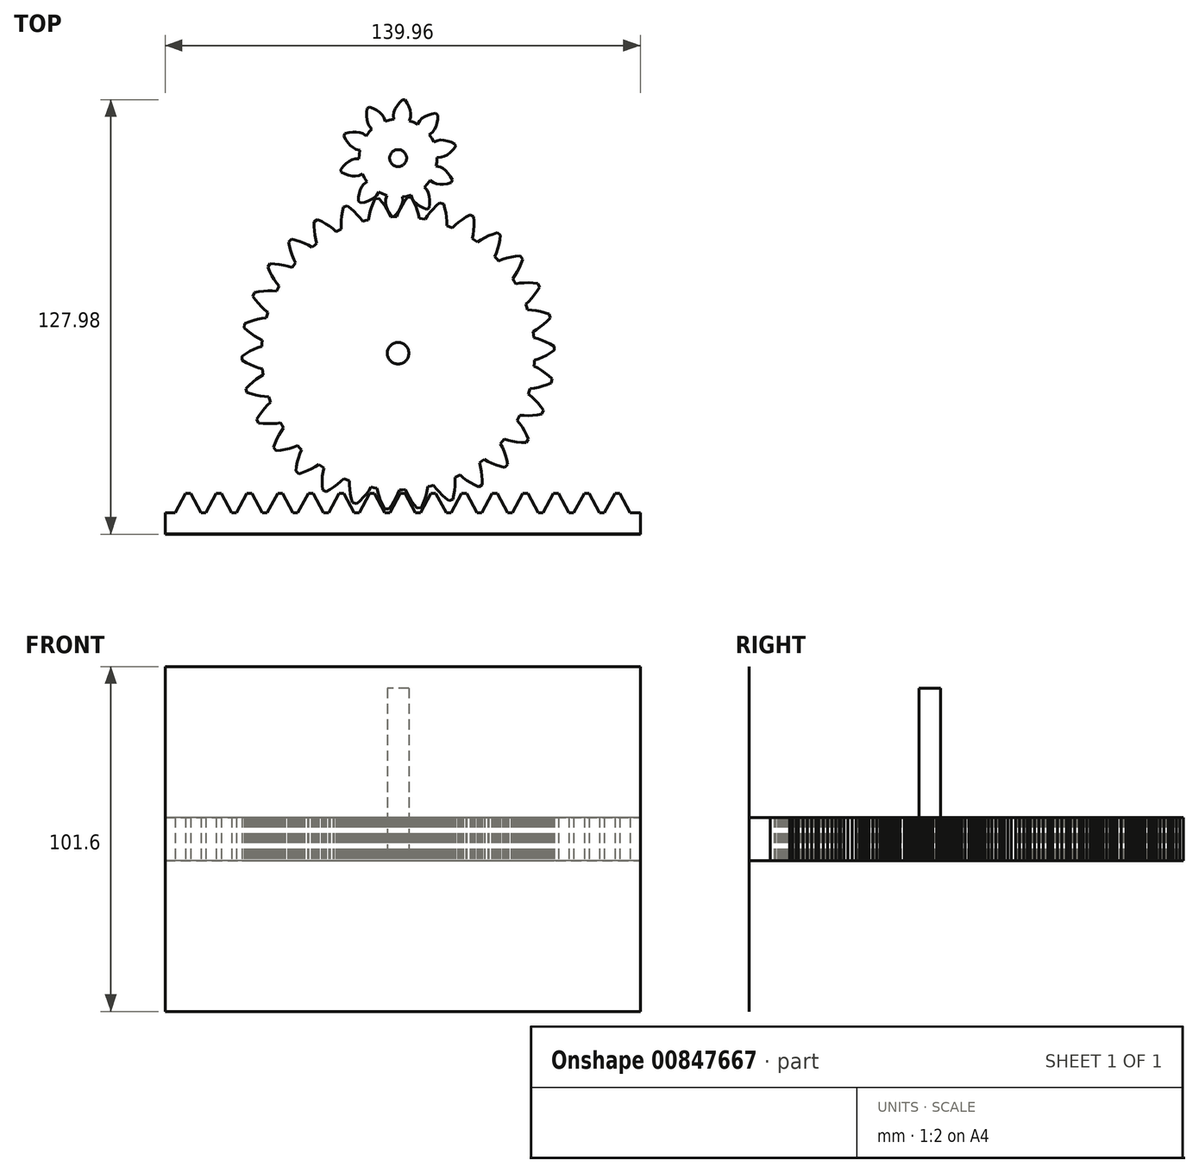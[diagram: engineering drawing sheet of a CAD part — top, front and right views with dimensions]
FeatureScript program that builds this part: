
annotation { "Feature Type Name" : "Feature", "Feature Type Description" : "" }
export const myFeature = defineFeature(function(context is Context, id is Id, definition is map)
    precondition{}
    {
        {
            var Q0;
            Q0=qCreatedBy(makeId("Top.planeOp"),FACE);
            var sketch = newSketch(context, id + "F0", { "sketchPlane" : qUnion([Q0])});
            skLineSegment(sketch, "E0", {"start": v(-1.74, 30.45) * mm, "end": v(-1.05, 31.36) * mm});
            skLineSegment(sketch, "E1", {"start": v(-1.05, 31.36) * mm, "end": v(-0.52, 32.3) * mm});
            skLineSegment(sketch, "E2", {"start": v(-0.52, 32.3) * mm, "end": v(-0.16, 33.24) * mm});
            skLineSegment(sketch, "E3", {"start": v(-0.16, 33.24) * mm, "end": v(-0.01, 34.16) * mm});
            skLineSegment(sketch, "E4", {"start": v(-0.01, 34.16) * mm, "end": v(-0.14, 35.35) * mm});
            skLineSegment(sketch, "E5", {"start": v(-0.14, 35.35) * mm, "end": v(1.13, 35.56) * mm});
            skLineSegment(sketch, "E6", {"start": v(1.13, 35.56) * mm, "end": v(1.13, 35.56) * mm});
            skLineSegment(sketch, "E7", {"start": v(1.13, 35.56) * mm, "end": v(1.15, 35.56) * mm});
            skLineSegment(sketch, "E8", {"start": v(1.15, 35.56) * mm, "end": v(1.17, 35.57) * mm});
            skLineSegment(sketch, "E9", {"start": v(1.17, 35.57) * mm, "end": v(1.17, 35.57) * mm});
            skLineSegment(sketch, "E10", {"start": v(1.17, 35.57) * mm, "end": v(2.41, 35.92) * mm});
            skLineSegment(sketch, "E11", {"start": v(2.41, 35.92) * mm, "end": v(2.8, 34.8) * mm});
            skLineSegment(sketch, "E12", {"start": v(2.8, 34.8) * mm, "end": v(3.33, 34.01) * mm});
            skLineSegment(sketch, "E13", {"start": v(3.33, 34.01) * mm, "end": v(4.06, 33.32) * mm});
            skLineSegment(sketch, "E14", {"start": v(4.06, 33.32) * mm, "end": v(4.94, 32.7) * mm});
            skLineSegment(sketch, "E15", {"start": v(4.94, 32.7) * mm, "end": v(5.95, 32.17) * mm});
            skLineSegment(sketch, "E16", {"start": v(5.95, 32.17) * mm, "end": v(7.07, 31.73) * mm});
            skLineSegment(sketch, "E17", {"start": v(7.07, 31.73) * mm, "end": v(7.77, 32.15) * mm});
            skLineSegment(sketch, "E18", {"start": v(7.77, 32.15) * mm, "end": v(7.93, 33.35) * mm});
            skLineSegment(sketch, "E19", {"start": v(7.93, 33.35) * mm, "end": v(7.95, 34.48) * mm});
            skLineSegment(sketch, "E20", {"start": v(7.95, 34.48) * mm, "end": v(7.84, 35.55) * mm});
            skLineSegment(sketch, "E21", {"start": v(7.84, 35.55) * mm, "end": v(7.58, 36.53) * mm});
            skLineSegment(sketch, "E22", {"start": v(7.58, 36.53) * mm, "end": v(7.15, 37.36) * mm});
            skLineSegment(sketch, "E23", {"start": v(7.15, 37.36) * mm, "end": v(6.35, 38.25) * mm});
            skLineSegment(sketch, "E24", {"start": v(6.35, 38.25) * mm, "end": v(7.25, 39.17) * mm});
            skLineSegment(sketch, "E25", {"start": v(7.25, 39.17) * mm, "end": v(7.26, 39.16) * mm});
            skLineSegment(sketch, "E26", {"start": v(7.26, 39.16) * mm, "end": v(7.27, 39.18) * mm});
            skLineSegment(sketch, "E27", {"start": v(7.27, 39.18) * mm, "end": v(7.28, 39.2) * mm});
            skLineSegment(sketch, "E28", {"start": v(7.28, 39.2) * mm, "end": v(7.28, 39.2) * mm});
            skLineSegment(sketch, "E29", {"start": v(7.28, 39.2) * mm, "end": v(8.08, 40.21) * mm});
            skLineSegment(sketch, "E30", {"start": v(8.08, 40.21) * mm, "end": v(9.06, 39.53) * mm});
            skLineSegment(sketch, "E31", {"start": v(9.06, 39.53) * mm, "end": v(9.94, 39.2) * mm});
            skLineSegment(sketch, "E32", {"start": v(9.94, 39.2) * mm, "end": v(10.94, 39.07) * mm});
            skLineSegment(sketch, "E33", {"start": v(10.94, 39.07) * mm, "end": v(12.01, 39.09) * mm});
            skLineSegment(sketch, "E34", {"start": v(12.01, 39.09) * mm, "end": v(13.14, 39.25) * mm});
            skLineSegment(sketch, "E35", {"start": v(13.14, 39.25) * mm, "end": v(14.3, 39.56) * mm});
            skLineSegment(sketch, "E36", {"start": v(14.3, 39.56) * mm, "end": v(14.63, 40.31) * mm});
            skLineSegment(sketch, "E37", {"start": v(14.63, 40.31) * mm, "end": v(14.06, 41.37) * mm});
            skLineSegment(sketch, "E38", {"start": v(14.06, 41.37) * mm, "end": v(13.4, 42.3) * mm});
            skLineSegment(sketch, "E39", {"start": v(13.4, 42.3) * mm, "end": v(12.68, 43.1) * mm});
            skLineSegment(sketch, "E40", {"start": v(12.68, 43.1) * mm, "end": v(11.9, 43.74) * mm});
            skLineSegment(sketch, "E41", {"start": v(11.9, 43.74) * mm, "end": v(11.06, 44.16) * mm});
            skLineSegment(sketch, "E42", {"start": v(11.06, 44.16) * mm, "end": v(9.9, 44.4) * mm});
            skLineSegment(sketch, "E43", {"start": v(9.9, 44.4) * mm, "end": v(10.09, 45.68) * mm});
            skLineSegment(sketch, "E44", {"start": v(10.09, 45.68) * mm, "end": v(10.09, 45.68) * mm});
            skLineSegment(sketch, "E45", {"start": v(10.09, 45.68) * mm, "end": v(10.1, 45.7) * mm});
            skLineSegment(sketch, "E46", {"start": v(10.1, 45.7) * mm, "end": v(10.1, 45.72) * mm});
            skLineSegment(sketch, "E47", {"start": v(10.1, 45.72) * mm, "end": v(10.1, 45.72) * mm});
            skLineSegment(sketch, "E48", {"start": v(10.1, 45.72) * mm, "end": v(10.14, 47.01) * mm});
            skLineSegment(sketch, "E49", {"start": v(10.14, 47.01) * mm, "end": v(11.33, 47.03) * mm});
            skLineSegment(sketch, "E50", {"start": v(11.33, 47.03) * mm, "end": v(12.24, 47.3) * mm});
            skLineSegment(sketch, "E51", {"start": v(12.24, 47.3) * mm, "end": v(13.12, 47.77) * mm});
            skLineSegment(sketch, "E52", {"start": v(13.12, 47.77) * mm, "end": v(13.98, 48.42) * mm});
            skLineSegment(sketch, "E53", {"start": v(13.98, 48.42) * mm, "end": v(14.8, 49.21) * mm});
            skLineSegment(sketch, "E54", {"start": v(14.8, 49.21) * mm, "end": v(15.56, 50.14) * mm});
            skLineSegment(sketch, "E55", {"start": v(15.56, 50.14) * mm, "end": v(15.38, 50.94) * mm});
            skLineSegment(sketch, "E56", {"start": v(15.38, 50.94) * mm, "end": v(14.3, 51.46) * mm});
            skLineSegment(sketch, "E57", {"start": v(14.3, 51.46) * mm, "end": v(13.22, 51.83) * mm});
            skLineSegment(sketch, "E58", {"start": v(13.22, 51.83) * mm, "end": v(12.17, 52.05) * mm});
            skLineSegment(sketch, "E59", {"start": v(12.17, 52.05) * mm, "end": v(11.16, 52.1) * mm});
            skLineSegment(sketch, "E60", {"start": v(11.16, 52.1) * mm, "end": v(10.23, 51.96) * mm});
            skLineSegment(sketch, "E61", {"start": v(10.23, 51.96) * mm, "end": v(9.14, 51.47) * mm});
            skLineSegment(sketch, "E62", {"start": v(9.14, 51.47) * mm, "end": v(8.55, 52.62) * mm});
            skLineSegment(sketch, "E63", {"start": v(8.55, 52.62) * mm, "end": v(8.55, 52.62) * mm});
            skLineSegment(sketch, "E64", {"start": v(8.55, 52.62) * mm, "end": v(8.54, 52.63) * mm});
            skLineSegment(sketch, "E65", {"start": v(8.54, 52.63) * mm, "end": v(8.53, 52.65) * mm});
            skLineSegment(sketch, "E66", {"start": v(8.53, 52.65) * mm, "end": v(8.53, 52.65) * mm});
            skLineSegment(sketch, "E67", {"start": v(8.53, 52.65) * mm, "end": v(7.81, 53.72) * mm});
            skLineSegment(sketch, "E68", {"start": v(7.81, 53.72) * mm, "end": v(8.76, 54.44) * mm});
            skLineSegment(sketch, "E69", {"start": v(8.76, 54.44) * mm, "end": v(9.34, 55.18) * mm});
            skLineSegment(sketch, "E70", {"start": v(9.34, 55.18) * mm, "end": v(9.78, 56.1) * mm});
            skLineSegment(sketch, "E71", {"start": v(9.78, 56.1) * mm, "end": v(10.1, 57.12) * mm});
            skLineSegment(sketch, "E72", {"start": v(10.1, 57.12) * mm, "end": v(10.29, 58.24) * mm});
            skLineSegment(sketch, "E73", {"start": v(10.29, 58.24) * mm, "end": v(10.35, 59.44) * mm});
            skLineSegment(sketch, "E74", {"start": v(10.35, 59.44) * mm, "end": v(9.74, 59.98) * mm});
            skLineSegment(sketch, "E75", {"start": v(9.74, 59.98) * mm, "end": v(8.56, 59.77) * mm});
            skLineSegment(sketch, "E76", {"start": v(8.56, 59.77) * mm, "end": v(7.47, 59.43) * mm});
            skLineSegment(sketch, "E77", {"start": v(7.47, 59.43) * mm, "end": v(6.49, 59) * mm});
            skLineSegment(sketch, "E78", {"start": v(6.49, 59) * mm, "end": v(5.64, 58.45) * mm});
            skLineSegment(sketch, "E79", {"start": v(5.64, 58.45) * mm, "end": v(4.98, 57.78) * mm});
            skLineSegment(sketch, "E80", {"start": v(4.98, 57.78) * mm, "end": v(4.38, 56.75) * mm});
            skLineSegment(sketch, "E81", {"start": v(4.38, 56.75) * mm, "end": v(3.23, 57.32) * mm});
            skLineSegment(sketch, "E82", {"start": v(3.23, 57.32) * mm, "end": v(3.23, 57.33) * mm});
            skLineSegment(sketch, "E83", {"start": v(3.23, 57.33) * mm, "end": v(3.21, 57.33) * mm});
            skLineSegment(sketch, "E84", {"start": v(3.21, 57.33) * mm, "end": v(3.2, 57.34) * mm});
            skLineSegment(sketch, "E85", {"start": v(3.2, 57.34) * mm, "end": v(3.2, 57.34) * mm});
            skLineSegment(sketch, "E86", {"start": v(3.2, 57.34) * mm, "end": v(1.98, 57.78) * mm});
            skLineSegment(sketch, "E87", {"start": v(1.98, 57.78) * mm, "end": v(2.33, 58.93) * mm});
            skLineSegment(sketch, "E88", {"start": v(2.33, 58.93) * mm, "end": v(2.36, 59.87) * mm});
            skLineSegment(sketch, "E89", {"start": v(2.36, 59.87) * mm, "end": v(2.18, 60.86) * mm});
            skLineSegment(sketch, "E90", {"start": v(2.18, 60.86) * mm, "end": v(1.83, 61.87) * mm});
            skLineSegment(sketch, "E91", {"start": v(1.83, 61.87) * mm, "end": v(1.33, 62.9) * mm});
            skLineSegment(sketch, "E92", {"start": v(1.33, 62.9) * mm, "end": v(0.67, 63.9) * mm});
            skLineSegment(sketch, "E93", {"start": v(0.67, 63.9) * mm, "end": v(-0.14, 63.99) * mm});
            skLineSegment(sketch, "E94", {"start": v(-0.14, 63.99) * mm, "end": v(-0.97, 63.11) * mm});
            skLineSegment(sketch, "E95", {"start": v(-0.97, 63.11) * mm, "end": v(-1.66, 62.2) * mm});
            skLineSegment(sketch, "E96", {"start": v(-1.66, 62.2) * mm, "end": v(-2.19, 61.27) * mm});
            skLineSegment(sketch, "E97", {"start": v(-2.19, 61.27) * mm, "end": v(-2.55, 60.33) * mm});
            skLineSegment(sketch, "E98", {"start": v(-2.55, 60.33) * mm, "end": v(-2.7, 59.4) * mm});
            skLineSegment(sketch, "E99", {"start": v(-2.7, 59.4) * mm, "end": v(-2.57, 58.22) * mm});
            skLineSegment(sketch, "E100", {"start": v(-2.57, 58.22) * mm, "end": v(-3.84, 58) * mm});
            skLineSegment(sketch, "E101", {"start": v(-3.84, 58) * mm, "end": v(-3.84, 58) * mm});
            skLineSegment(sketch, "E102", {"start": v(-3.84, 58) * mm, "end": v(-3.86, 58) * mm});
            skLineSegment(sketch, "E103", {"start": v(-3.86, 58) * mm, "end": v(-3.88, 58) * mm});
            skLineSegment(sketch, "E104", {"start": v(-3.88, 58) * mm, "end": v(-3.88, 58) * mm});
            skLineSegment(sketch, "E105", {"start": v(-3.88, 58) * mm, "end": v(-5.12, 57.64) * mm});
            skLineSegment(sketch, "E106", {"start": v(-5.12, 57.64) * mm, "end": v(-5.51, 58.77) * mm});
            skLineSegment(sketch, "E107", {"start": v(-5.51, 58.77) * mm, "end": v(-6.04, 59.55) * mm});
            skLineSegment(sketch, "E108", {"start": v(-6.04, 59.55) * mm, "end": v(-6.77, 60.25) * mm});
            skLineSegment(sketch, "E109", {"start": v(-6.77, 60.25) * mm, "end": v(-7.65, 60.86) * mm});
            skLineSegment(sketch, "E110", {"start": v(-7.65, 60.86) * mm, "end": v(-8.66, 61.4) * mm});
            skLineSegment(sketch, "E111", {"start": v(-8.66, 61.4) * mm, "end": v(-9.78, 61.83) * mm});
            skLineSegment(sketch, "E112", {"start": v(-9.78, 61.83) * mm, "end": v(-10.48, 61.41) * mm});
            skLineSegment(sketch, "E113", {"start": v(-10.48, 61.41) * mm, "end": v(-10.64, 60.22) * mm});
            skLineSegment(sketch, "E114", {"start": v(-10.64, 60.22) * mm, "end": v(-10.66, 59.08) * mm});
            skLineSegment(sketch, "E115", {"start": v(-10.66, 59.08) * mm, "end": v(-10.55, 58.01) * mm});
            skLineSegment(sketch, "E116", {"start": v(-10.55, 58.01) * mm, "end": v(-10.29, 57.04) * mm});
            skLineSegment(sketch, "E117", {"start": v(-10.29, 57.04) * mm, "end": v(-9.86, 56.2) * mm});
            skLineSegment(sketch, "E118", {"start": v(-9.86, 56.2) * mm, "end": v(-9.06, 55.32) * mm});
            skLineSegment(sketch, "E119", {"start": v(-9.06, 55.32) * mm, "end": v(-9.96, 54.4) * mm});
            skLineSegment(sketch, "E120", {"start": v(-9.96, 54.4) * mm, "end": v(-9.97, 54.4) * mm});
            skLineSegment(sketch, "E121", {"start": v(-9.97, 54.4) * mm, "end": v(-9.98, 54.38) * mm});
            skLineSegment(sketch, "E122", {"start": v(-9.98, 54.38) * mm, "end": v(-10, 54.37) * mm});
            skLineSegment(sketch, "E123", {"start": v(-10, 54.37) * mm, "end": v(-10, 54.37) * mm});
            skLineSegment(sketch, "E124", {"start": v(-10, 54.37) * mm, "end": v(-10.79, 53.35) * mm});
            skLineSegment(sketch, "E125", {"start": v(-10.79, 53.35) * mm, "end": v(-11.77, 54.04) * mm});
            skLineSegment(sketch, "E126", {"start": v(-11.77, 54.04) * mm, "end": v(-12.65, 54.36) * mm});
            skLineSegment(sketch, "E127", {"start": v(-12.65, 54.36) * mm, "end": v(-13.65, 54.5) * mm});
            skLineSegment(sketch, "E128", {"start": v(-13.65, 54.5) * mm, "end": v(-14.72, 54.48) * mm});
            skLineSegment(sketch, "E129", {"start": v(-14.72, 54.48) * mm, "end": v(-15.85, 54.31) * mm});
            skLineSegment(sketch, "E130", {"start": v(-15.85, 54.31) * mm, "end": v(-17.02, 54) * mm});
            skLineSegment(sketch, "E131", {"start": v(-17.02, 54) * mm, "end": v(-17.34, 53.25) * mm});
            skLineSegment(sketch, "E132", {"start": v(-17.34, 53.25) * mm, "end": v(-16.77, 52.2) * mm});
            skLineSegment(sketch, "E133", {"start": v(-16.77, 52.2) * mm, "end": v(-16.11, 51.26) * mm});
            skLineSegment(sketch, "E134", {"start": v(-16.11, 51.26) * mm, "end": v(-15.4, 50.47) * mm});
            skLineSegment(sketch, "E135", {"start": v(-15.4, 50.47) * mm, "end": v(-14.6, 49.83) * mm});
            skLineSegment(sketch, "E136", {"start": v(-14.6, 49.83) * mm, "end": v(-13.77, 49.4) * mm});
            skLineSegment(sketch, "E137", {"start": v(-13.77, 49.4) * mm, "end": v(-12.6, 49.16) * mm});
            skLineSegment(sketch, "E138", {"start": v(-12.6, 49.16) * mm, "end": v(-12.8, 47.88) * mm});
            skLineSegment(sketch, "E139", {"start": v(-12.8, 47.88) * mm, "end": v(-12.8, 47.88) * mm});
            skLineSegment(sketch, "E140", {"start": v(-12.8, 47.88) * mm, "end": v(-12.8, 47.86) * mm});
            skLineSegment(sketch, "E141", {"start": v(-12.8, 47.86) * mm, "end": v(-12.8, 47.84) * mm});
            skLineSegment(sketch, "E142", {"start": v(-12.8, 47.84) * mm, "end": v(-12.8, 47.84) * mm});
            skLineSegment(sketch, "E143", {"start": v(-12.8, 47.84) * mm, "end": v(-12.85, 46.55) * mm});
            skLineSegment(sketch, "E144", {"start": v(-12.85, 46.55) * mm, "end": v(-14.04, 46.53) * mm});
            skLineSegment(sketch, "E145", {"start": v(-14.04, 46.53) * mm, "end": v(-14.95, 46.27) * mm});
            skLineSegment(sketch, "E146", {"start": v(-14.95, 46.27) * mm, "end": v(-15.83, 45.8) * mm});
            skLineSegment(sketch, "E147", {"start": v(-15.83, 45.8) * mm, "end": v(-16.7, 45.15) * mm});
            skLineSegment(sketch, "E148", {"start": v(-16.7, 45.15) * mm, "end": v(-17.5, 44.35) * mm});
            skLineSegment(sketch, "E149", {"start": v(-17.5, 44.35) * mm, "end": v(-18.27, 43.42) * mm});
            skLineSegment(sketch, "E150", {"start": v(-18.27, 43.42) * mm, "end": v(-18.1, 42.62) * mm});
            skLineSegment(sketch, "E151", {"start": v(-18.1, 42.62) * mm, "end": v(-17, 42.1) * mm});
            skLineSegment(sketch, "E152", {"start": v(-17, 42.1) * mm, "end": v(-15.93, 41.73) * mm});
            skLineSegment(sketch, "E153", {"start": v(-15.93, 41.73) * mm, "end": v(-14.88, 41.51) * mm});
            skLineSegment(sketch, "E154", {"start": v(-14.88, 41.51) * mm, "end": v(-13.87, 41.46) * mm});
            skLineSegment(sketch, "E155", {"start": v(-13.87, 41.46) * mm, "end": v(-12.94, 41.6) * mm});
            skLineSegment(sketch, "E156", {"start": v(-12.94, 41.6) * mm, "end": v(-11.85, 42.1) * mm});
            skLineSegment(sketch, "E157", {"start": v(-11.85, 42.1) * mm, "end": v(-11.26, 40.95) * mm});
            skLineSegment(sketch, "E158", {"start": v(-11.26, 40.95) * mm, "end": v(-11.26, 40.95) * mm});
            skLineSegment(sketch, "E159", {"start": v(-11.26, 40.95) * mm, "end": v(-11.25, 40.93) * mm});
            skLineSegment(sketch, "E160", {"start": v(-11.25, 40.93) * mm, "end": v(-11.24, 40.91) * mm});
            skLineSegment(sketch, "E161", {"start": v(-11.24, 40.91) * mm, "end": v(-11.24, 40.91) * mm});
            skLineSegment(sketch, "E162", {"start": v(-11.24, 40.91) * mm, "end": v(-10.52, 39.84) * mm});
            skLineSegment(sketch, "E163", {"start": v(-10.52, 39.84) * mm, "end": v(-11.47, 39.12) * mm});
            skLineSegment(sketch, "E164", {"start": v(-11.47, 39.12) * mm, "end": v(-12.05, 38.38) * mm});
            skLineSegment(sketch, "E165", {"start": v(-12.05, 38.38) * mm, "end": v(-12.49, 37.47) * mm});
            skLineSegment(sketch, "E166", {"start": v(-12.49, 37.47) * mm, "end": v(-12.8, 36.45) * mm});
            skLineSegment(sketch, "E167", {"start": v(-12.8, 36.45) * mm, "end": v(-13, 35.32) * mm});
            skLineSegment(sketch, "E168", {"start": v(-13, 35.32) * mm, "end": v(-13.06, 34.12) * mm});
            skLineSegment(sketch, "E169", {"start": v(-13.06, 34.12) * mm, "end": v(-12.45, 33.58) * mm});
            skLineSegment(sketch, "E170", {"start": v(-12.45, 33.58) * mm, "end": v(-11.26, 33.8) * mm});
            skLineSegment(sketch, "E171", {"start": v(-11.26, 33.8) * mm, "end": v(-10.17, 34.13) * mm});
            skLineSegment(sketch, "E172", {"start": v(-10.17, 34.13) * mm, "end": v(-9.2, 34.57) * mm});
            skLineSegment(sketch, "E173", {"start": v(-9.2, 34.57) * mm, "end": v(-8.35, 35.12) * mm});
            skLineSegment(sketch, "E174", {"start": v(-8.35, 35.12) * mm, "end": v(-7.69, 35.79) * mm});
            skLineSegment(sketch, "E175", {"start": v(-7.69, 35.79) * mm, "end": v(-7.1, 36.82) * mm});
            skLineSegment(sketch, "E176", {"start": v(-7.1, 36.82) * mm, "end": v(-5.94, 36.24) * mm});
            skLineSegment(sketch, "E177", {"start": v(-5.94, 36.24) * mm, "end": v(-5.94, 36.24) * mm});
            skLineSegment(sketch, "E178", {"start": v(-5.94, 36.24) * mm, "end": v(-5.92, 36.23) * mm});
            skLineSegment(sketch, "E179", {"start": v(-5.92, 36.23) * mm, "end": v(-5.9, 36.22) * mm});
            skLineSegment(sketch, "E180", {"start": v(-5.9, 36.22) * mm, "end": v(-5.9, 36.23) * mm});
            skLineSegment(sketch, "E181", {"start": v(-5.9, 36.23) * mm, "end": v(-4.69, 35.78) * mm});
            skLineSegment(sketch, "E182", {"start": v(-4.69, 35.78) * mm, "end": v(-5.04, 34.64) * mm});
            skLineSegment(sketch, "E183", {"start": v(-5.04, 34.64) * mm, "end": v(-5.07, 33.7) * mm});
            skLineSegment(sketch, "E184", {"start": v(-5.07, 33.7) * mm, "end": v(-4.89, 32.7) * mm});
            skLineSegment(sketch, "E185", {"start": v(-4.89, 32.7) * mm, "end": v(-4.54, 31.7) * mm});
            skLineSegment(sketch, "E186", {"start": v(-4.54, 31.7) * mm, "end": v(-4.04, 30.67) * mm});
            skLineSegment(sketch, "E187", {"start": v(-4.04, 30.67) * mm, "end": v(-3.38, 29.66) * mm});
            skLineSegment(sketch, "E188", {"start": v(-3.38, 29.66) * mm, "end": v(-2.57, 29.58) * mm});
            skLineSegment(sketch, "E189", {"start": v(-2.57, 29.58) * mm, "end": v(-1.74, 30.45) * mm});
            skLineSegment(sketch, "E190", {"start": v(-3.3, -55.5) * mm, "end": v(-2.59, -54.37) * mm});
            skLineSegment(sketch, "E191", {"start": v(-2.59, -54.37) * mm, "end": v(-1.95, -53.24) * mm});
            skLineSegment(sketch, "E192", {"start": v(-1.95, -53.24) * mm, "end": v(-1.4, -52.1) * mm});
            skLineSegment(sketch, "E193", {"start": v(-1.4, -52.1) * mm, "end": v(-0.97, -50.94) * mm});
            skLineSegment(sketch, "E194", {"start": v(-0.97, -50.94) * mm, "end": v(-0.07, -50.92) * mm});
            skLineSegment(sketch, "E195", {"start": v(-0.07, -50.92) * mm, "end": v(0.79, -50.88) * mm});
            skLineSegment(sketch, "E196", {"start": v(0.79, -50.88) * mm, "end": v(1.3, -52) * mm});
            skLineSegment(sketch, "E197", {"start": v(1.3, -52) * mm, "end": v(1.91, -53.12) * mm});
            skLineSegment(sketch, "E198", {"start": v(1.91, -53.12) * mm, "end": v(2.62, -54.21) * mm});
            skLineSegment(sketch, "E199", {"start": v(2.62, -54.21) * mm, "end": v(3.4, -55.29) * mm});
            skLineSegment(sketch, "E200", {"start": v(3.4, -55.29) * mm, "end": v(4.28, -56.34) * mm});
            skLineSegment(sketch, "E201", {"start": v(4.28, -56.34) * mm, "end": v(5.49, -56.18) * mm});
            skLineSegment(sketch, "E202", {"start": v(5.49, -56.18) * mm, "end": v(6.05, -54.93) * mm});
            skLineSegment(sketch, "E203", {"start": v(6.05, -54.93) * mm, "end": v(6.52, -53.68) * mm});
            skLineSegment(sketch, "E204", {"start": v(6.52, -53.68) * mm, "end": v(6.9, -52.43) * mm});
            skLineSegment(sketch, "E205", {"start": v(6.9, -52.43) * mm, "end": v(7.2, -51.2) * mm});
            skLineSegment(sketch, "E206", {"start": v(7.2, -51.2) * mm, "end": v(7.39, -49.98) * mm});
            skLineSegment(sketch, "E207", {"start": v(7.39, -49.98) * mm, "end": v(8.27, -49.77) * mm});
            skLineSegment(sketch, "E208", {"start": v(8.27, -49.77) * mm, "end": v(9.1, -49.56) * mm});
            skLineSegment(sketch, "E209", {"start": v(9.1, -49.56) * mm, "end": v(9.83, -50.55) * mm});
            skLineSegment(sketch, "E210", {"start": v(9.83, -50.55) * mm, "end": v(10.66, -51.5) * mm});
            skLineSegment(sketch, "E211", {"start": v(10.66, -51.5) * mm, "end": v(11.58, -52.43) * mm});
            skLineSegment(sketch, "E212", {"start": v(11.58, -52.43) * mm, "end": v(12.57, -53.32) * mm});
            skLineSegment(sketch, "E213", {"start": v(12.57, -53.32) * mm, "end": v(13.65, -54.17) * mm});
            skLineSegment(sketch, "E214", {"start": v(13.65, -54.17) * mm, "end": v(14.8, -53.76) * mm});
            skLineSegment(sketch, "E215", {"start": v(14.8, -53.76) * mm, "end": v(15.08, -52.42) * mm});
            skLineSegment(sketch, "E216", {"start": v(15.08, -52.42) * mm, "end": v(15.28, -51.1) * mm});
            skLineSegment(sketch, "E217", {"start": v(15.28, -51.1) * mm, "end": v(15.4, -49.8) * mm});
            skLineSegment(sketch, "E218", {"start": v(15.4, -49.8) * mm, "end": v(15.43, -48.54) * mm});
            skLineSegment(sketch, "E219", {"start": v(15.43, -48.54) * mm, "end": v(15.36, -47.3) * mm});
            skLineSegment(sketch, "E220", {"start": v(15.36, -47.3) * mm, "end": v(16.18, -46.92) * mm});
            skLineSegment(sketch, "E221", {"start": v(16.18, -46.92) * mm, "end": v(16.95, -46.54) * mm});
            skLineSegment(sketch, "E222", {"start": v(16.95, -46.54) * mm, "end": v(17.87, -47.36) * mm});
            skLineSegment(sketch, "E223", {"start": v(17.87, -47.36) * mm, "end": v(18.88, -48.12) * mm});
            skLineSegment(sketch, "E224", {"start": v(18.88, -48.12) * mm, "end": v(19.97, -48.83) * mm});
            skLineSegment(sketch, "E225", {"start": v(19.97, -48.83) * mm, "end": v(21.13, -49.5) * mm});
            skLineSegment(sketch, "E226", {"start": v(21.13, -49.5) * mm, "end": v(22.36, -50.1) * mm});
            skLineSegment(sketch, "E227", {"start": v(22.36, -50.1) * mm, "end": v(23.4, -49.46) * mm});
            skLineSegment(sketch, "E228", {"start": v(23.4, -49.46) * mm, "end": v(23.4, -48.1) * mm});
            skLineSegment(sketch, "E229", {"start": v(23.4, -48.1) * mm, "end": v(23.32, -46.76) * mm});
            skLineSegment(sketch, "E230", {"start": v(23.32, -46.76) * mm, "end": v(23.16, -45.46) * mm});
            skLineSegment(sketch, "E231", {"start": v(23.16, -45.46) * mm, "end": v(22.93, -44.22) * mm});
            skLineSegment(sketch, "E232", {"start": v(22.93, -44.22) * mm, "end": v(22.6, -43.03) * mm});
            skLineSegment(sketch, "E233", {"start": v(22.6, -43.03) * mm, "end": v(23.33, -42.48) * mm});
            skLineSegment(sketch, "E234", {"start": v(23.33, -42.48) * mm, "end": v(24, -41.95) * mm});
            skLineSegment(sketch, "E235", {"start": v(24, -41.95) * mm, "end": v(25.07, -42.56) * mm});
            skLineSegment(sketch, "E236", {"start": v(25.07, -42.56) * mm, "end": v(26.22, -43.1) * mm});
            skLineSegment(sketch, "E237", {"start": v(26.22, -43.1) * mm, "end": v(27.43, -43.57) * mm});
            skLineSegment(sketch, "E238", {"start": v(27.43, -43.57) * mm, "end": v(28.7, -43.97) * mm});
            skLineSegment(sketch, "E239", {"start": v(28.7, -43.97) * mm, "end": v(30.03, -44.31) * mm});
            skLineSegment(sketch, "E240", {"start": v(30.03, -44.31) * mm, "end": v(30.91, -43.47) * mm});
            skLineSegment(sketch, "E241", {"start": v(30.91, -43.47) * mm, "end": v(30.63, -42.13) * mm});
            skLineSegment(sketch, "E242", {"start": v(30.63, -42.13) * mm, "end": v(30.28, -40.84) * mm});
            skLineSegment(sketch, "E243", {"start": v(30.28, -40.84) * mm, "end": v(29.86, -39.6) * mm});
            skLineSegment(sketch, "E244", {"start": v(29.86, -39.6) * mm, "end": v(29.37, -38.44) * mm});
            skLineSegment(sketch, "E245", {"start": v(29.37, -38.44) * mm, "end": v(28.8, -37.34) * mm});
            skLineSegment(sketch, "E246", {"start": v(28.8, -37.34) * mm, "end": v(29.4, -36.66) * mm});
            skLineSegment(sketch, "E247", {"start": v(29.4, -36.66) * mm, "end": v(29.94, -36) * mm});
            skLineSegment(sketch, "E248", {"start": v(29.94, -36) * mm, "end": v(31.12, -36.37) * mm});
            skLineSegment(sketch, "E249", {"start": v(31.12, -36.37) * mm, "end": v(32.35, -36.66) * mm});
            skLineSegment(sketch, "E250", {"start": v(32.35, -36.66) * mm, "end": v(33.64, -36.86) * mm});
            skLineSegment(sketch, "E251", {"start": v(33.64, -36.86) * mm, "end": v(34.97, -37) * mm});
            skLineSegment(sketch, "E252", {"start": v(34.97, -37) * mm, "end": v(36.34, -37.05) * mm});
            skLineSegment(sketch, "E253", {"start": v(36.34, -37.05) * mm, "end": v(37.02, -36.05) * mm});
            skLineSegment(sketch, "E254", {"start": v(37.02, -36.05) * mm, "end": v(36.46, -34.8) * mm});
            skLineSegment(sketch, "E255", {"start": v(36.46, -34.8) * mm, "end": v(35.85, -33.6) * mm});
            skLineSegment(sketch, "E256", {"start": v(35.85, -33.6) * mm, "end": v(35.18, -32.49) * mm});
            skLineSegment(sketch, "E257", {"start": v(35.18, -32.49) * mm, "end": v(34.46, -31.44) * mm});
            skLineSegment(sketch, "E258", {"start": v(34.46, -31.44) * mm, "end": v(33.68, -30.49) * mm});
            skLineSegment(sketch, "E259", {"start": v(33.68, -30.49) * mm, "end": v(34.12, -29.7) * mm});
            skLineSegment(sketch, "E260", {"start": v(34.12, -29.7) * mm, "end": v(34.52, -28.94) * mm});
            skLineSegment(sketch, "E261", {"start": v(34.52, -28.94) * mm, "end": v(35.74, -29.06) * mm});
            skLineSegment(sketch, "E262", {"start": v(35.74, -29.06) * mm, "end": v(37, -29.08) * mm});
            skLineSegment(sketch, "E263", {"start": v(37, -29.08) * mm, "end": v(38.31, -29.02) * mm});
            skLineSegment(sketch, "E264", {"start": v(38.31, -29.02) * mm, "end": v(39.64, -28.87) * mm});
            skLineSegment(sketch, "E265", {"start": v(39.64, -28.87) * mm, "end": v(41, -28.64) * mm});
            skLineSegment(sketch, "E266", {"start": v(41, -28.64) * mm, "end": v(41.45, -27.51) * mm});
            skLineSegment(sketch, "E267", {"start": v(41.45, -27.51) * mm, "end": v(40.64, -26.4) * mm});
            skLineSegment(sketch, "E268", {"start": v(40.64, -26.4) * mm, "end": v(39.8, -25.37) * mm});
            skLineSegment(sketch, "E269", {"start": v(39.8, -25.37) * mm, "end": v(38.91, -24.41) * mm});
            skLineSegment(sketch, "E270", {"start": v(38.91, -24.41) * mm, "end": v(38, -23.54) * mm});
            skLineSegment(sketch, "E271", {"start": v(38, -23.54) * mm, "end": v(37.03, -22.77) * mm});
            skLineSegment(sketch, "E272", {"start": v(37.03, -22.77) * mm, "end": v(37.3, -21.9) * mm});
            skLineSegment(sketch, "E273", {"start": v(37.3, -21.9) * mm, "end": v(37.52, -21.08) * mm});
            skLineSegment(sketch, "E274", {"start": v(37.52, -21.08) * mm, "end": v(38.75, -20.94) * mm});
            skLineSegment(sketch, "E275", {"start": v(38.75, -20.94) * mm, "end": v(40, -20.7) * mm});
            skLineSegment(sketch, "E276", {"start": v(40, -20.7) * mm, "end": v(41.25, -20.37) * mm});
            skLineSegment(sketch, "E277", {"start": v(41.25, -20.37) * mm, "end": v(42.52, -19.95) * mm});
            skLineSegment(sketch, "E278", {"start": v(42.52, -19.95) * mm, "end": v(43.8, -19.44) * mm});
            skLineSegment(sketch, "E279", {"start": v(43.8, -19.44) * mm, "end": v(44.01, -18.25) * mm});
            skLineSegment(sketch, "E280", {"start": v(44.01, -18.25) * mm, "end": v(43, -17.33) * mm});
            skLineSegment(sketch, "E281", {"start": v(43, -17.33) * mm, "end": v(41.95, -16.5) * mm});
            skLineSegment(sketch, "E282", {"start": v(41.95, -16.5) * mm, "end": v(40.88, -15.74) * mm});
            skLineSegment(sketch, "E283", {"start": v(40.88, -15.74) * mm, "end": v(39.8, -15.08) * mm});
            skLineSegment(sketch, "E284", {"start": v(39.8, -15.08) * mm, "end": v(38.7, -14.53) * mm});
            skLineSegment(sketch, "E285", {"start": v(38.7, -14.53) * mm, "end": v(38.78, -13.63) * mm});
            skLineSegment(sketch, "E286", {"start": v(38.78, -13.63) * mm, "end": v(38.83, -12.77) * mm});
            skLineSegment(sketch, "E287", {"start": v(38.83, -12.77) * mm, "end": v(40, -12.38) * mm});
            skLineSegment(sketch, "E288", {"start": v(40, -12.38) * mm, "end": v(41.17, -11.89) * mm});
            skLineSegment(sketch, "E289", {"start": v(41.17, -11.89) * mm, "end": v(42.33, -11.3) * mm});
            skLineSegment(sketch, "E290", {"start": v(42.33, -11.3) * mm, "end": v(43.48, -10.63) * mm});
            skLineSegment(sketch, "E291", {"start": v(43.48, -10.63) * mm, "end": v(44.63, -9.87) * mm});
            skLineSegment(sketch, "E292", {"start": v(44.63, -9.87) * mm, "end": v(44.59, -8.65) * mm});
            skLineSegment(sketch, "E293", {"start": v(44.59, -8.65) * mm, "end": v(43.4, -7.96) * mm});
            skLineSegment(sketch, "E294", {"start": v(43.4, -7.96) * mm, "end": v(42.2, -7.36) * mm});
            skLineSegment(sketch, "E295", {"start": v(42.2, -7.36) * mm, "end": v(41, -6.85) * mm});
            skLineSegment(sketch, "E296", {"start": v(41, -6.85) * mm, "end": v(39.81, -6.43) * mm});
            skLineSegment(sketch, "E297", {"start": v(39.81, -6.43) * mm, "end": v(38.62, -6.11) * mm});
            skLineSegment(sketch, "E298", {"start": v(38.62, -6.11) * mm, "end": v(38.5, -5.22) * mm});
            skLineSegment(sketch, "E299", {"start": v(38.5, -5.22) * mm, "end": v(38.38, -4.37) * mm});
            skLineSegment(sketch, "E300", {"start": v(38.38, -4.37) * mm, "end": v(39.45, -3.75) * mm});
            skLineSegment(sketch, "E301", {"start": v(39.45, -3.75) * mm, "end": v(40.49, -3.02) * mm});
            skLineSegment(sketch, "E302", {"start": v(40.49, -3.02) * mm, "end": v(41.5, -2.2) * mm});
            skLineSegment(sketch, "E303", {"start": v(41.5, -2.2) * mm, "end": v(42.49, -1.3) * mm});
            skLineSegment(sketch, "E304", {"start": v(42.49, -1.3) * mm, "end": v(43.45, -0.33) * mm});
            skLineSegment(sketch, "E305", {"start": v(43.45, -0.33) * mm, "end": v(43.16, 0.86) * mm});
            skLineSegment(sketch, "E306", {"start": v(43.16, 0.86) * mm, "end": v(41.85, 1.28) * mm});
            skLineSegment(sketch, "E307", {"start": v(41.85, 1.28) * mm, "end": v(40.56, 1.62) * mm});
            skLineSegment(sketch, "E308", {"start": v(40.56, 1.62) * mm, "end": v(39.28, 1.87) * mm});
            skLineSegment(sketch, "E309", {"start": v(39.28, 1.87) * mm, "end": v(38.03, 2.03) * mm});
            skLineSegment(sketch, "E310", {"start": v(38.03, 2.03) * mm, "end": v(36.8, 2.1) * mm});
            skLineSegment(sketch, "E311", {"start": v(36.8, 2.1) * mm, "end": v(36.5, 2.95) * mm});
            skLineSegment(sketch, "E312", {"start": v(36.5, 2.95) * mm, "end": v(36.2, 3.75) * mm});
            skLineSegment(sketch, "E313", {"start": v(36.2, 3.75) * mm, "end": v(37.1, 4.59) * mm});
            skLineSegment(sketch, "E314", {"start": v(37.1, 4.59) * mm, "end": v(37.97, 5.51) * mm});
            skLineSegment(sketch, "E315", {"start": v(37.97, 5.51) * mm, "end": v(38.8, 6.52) * mm});
            skLineSegment(sketch, "E316", {"start": v(38.8, 6.52) * mm, "end": v(39.58, 7.6) * mm});
            skLineSegment(sketch, "E317", {"start": v(39.58, 7.6) * mm, "end": v(40.31, 8.76) * mm});
            skLineSegment(sketch, "E318", {"start": v(40.31, 8.76) * mm, "end": v(39.78, 9.86) * mm});
            skLineSegment(sketch, "E319", {"start": v(39.78, 9.86) * mm, "end": v(38.42, 10) * mm});
            skLineSegment(sketch, "E320", {"start": v(38.42, 10) * mm, "end": v(37.08, 10.07) * mm});
            skLineSegment(sketch, "E321", {"start": v(37.08, 10.07) * mm, "end": v(35.78, 10.05) * mm});
            skLineSegment(sketch, "E322", {"start": v(35.78, 10.05) * mm, "end": v(34.52, 9.94) * mm});
            skLineSegment(sketch, "E323", {"start": v(34.52, 9.94) * mm, "end": v(33.3, 9.75) * mm});
            skLineSegment(sketch, "E324", {"start": v(33.3, 9.75) * mm, "end": v(32.83, 10.52) * mm});
            skLineSegment(sketch, "E325", {"start": v(32.83, 10.52) * mm, "end": v(32.37, 11.24) * mm});
            skLineSegment(sketch, "E326", {"start": v(32.37, 11.24) * mm, "end": v(33.09, 12.25) * mm});
            skLineSegment(sketch, "E327", {"start": v(33.09, 12.25) * mm, "end": v(33.74, 13.33) * mm});
            skLineSegment(sketch, "E328", {"start": v(33.74, 13.33) * mm, "end": v(34.34, 14.5) * mm});
            skLineSegment(sketch, "E329", {"start": v(34.34, 14.5) * mm, "end": v(34.88, 15.71) * mm});
            skLineSegment(sketch, "E330", {"start": v(34.88, 15.71) * mm, "end": v(35.35, 17) * mm});
            skLineSegment(sketch, "E331", {"start": v(35.35, 17) * mm, "end": v(34.6, 17.96) * mm});
            skLineSegment(sketch, "E332", {"start": v(34.6, 17.96) * mm, "end": v(33.24, 17.82) * mm});
            skLineSegment(sketch, "E333", {"start": v(33.24, 17.82) * mm, "end": v(31.92, 17.6) * mm});
            skLineSegment(sketch, "E334", {"start": v(31.92, 17.6) * mm, "end": v(30.65, 17.32) * mm});
            skLineSegment(sketch, "E335", {"start": v(30.65, 17.32) * mm, "end": v(29.44, 16.95) * mm});
            skLineSegment(sketch, "E336", {"start": v(29.44, 16.95) * mm, "end": v(28.3, 16.5) * mm});
            skLineSegment(sketch, "E337", {"start": v(28.3, 16.5) * mm, "end": v(27.67, 17.17) * mm});
            skLineSegment(sketch, "E338", {"start": v(27.67, 17.17) * mm, "end": v(27.07, 17.78) * mm});
            skLineSegment(sketch, "E339", {"start": v(27.07, 17.78) * mm, "end": v(27.56, 18.9) * mm});
            skLineSegment(sketch, "E340", {"start": v(27.56, 18.9) * mm, "end": v(27.98, 20.1) * mm});
            skLineSegment(sketch, "E341", {"start": v(27.98, 20.1) * mm, "end": v(28.32, 21.36) * mm});
            skLineSegment(sketch, "E342", {"start": v(28.32, 21.36) * mm, "end": v(28.6, 22.67) * mm});
            skLineSegment(sketch, "E343", {"start": v(28.6, 22.67) * mm, "end": v(28.8, 24.03) * mm});
            skLineSegment(sketch, "E344", {"start": v(28.8, 24.03) * mm, "end": v(27.86, 24.81) * mm});
            skLineSegment(sketch, "E345", {"start": v(27.86, 24.81) * mm, "end": v(26.56, 24.39) * mm});
            skLineSegment(sketch, "E346", {"start": v(26.56, 24.39) * mm, "end": v(25.31, 23.9) * mm});
            skLineSegment(sketch, "E347", {"start": v(25.31, 23.9) * mm, "end": v(24.13, 23.36) * mm});
            skLineSegment(sketch, "E348", {"start": v(24.13, 23.36) * mm, "end": v(23.02, 22.75) * mm});
            skLineSegment(sketch, "E349", {"start": v(23.02, 22.75) * mm, "end": v(21.99, 22.08) * mm});
            skLineSegment(sketch, "E350", {"start": v(21.99, 22.08) * mm, "end": v(21.24, 22.6) * mm});
            skLineSegment(sketch, "E351", {"start": v(21.24, 22.6) * mm, "end": v(20.53, 23.07) * mm});
            skLineSegment(sketch, "E352", {"start": v(20.53, 23.07) * mm, "end": v(20.78, 24.27) * mm});
            skLineSegment(sketch, "E353", {"start": v(20.78, 24.27) * mm, "end": v(20.93, 25.53) * mm});
            skLineSegment(sketch, "E354", {"start": v(20.93, 25.53) * mm, "end": v(21, 26.83) * mm});
            skLineSegment(sketch, "E355", {"start": v(21, 26.83) * mm, "end": v(21, 28.17) * mm});
            skLineSegment(sketch, "E356", {"start": v(21, 28.17) * mm, "end": v(20.91, 29.54) * mm});
            skLineSegment(sketch, "E357", {"start": v(20.91, 29.54) * mm, "end": v(19.84, 30.11) * mm});
            skLineSegment(sketch, "E358", {"start": v(19.84, 30.11) * mm, "end": v(18.65, 29.43) * mm});
            skLineSegment(sketch, "E359", {"start": v(18.65, 29.43) * mm, "end": v(17.53, 28.7) * mm});
            skLineSegment(sketch, "E360", {"start": v(17.53, 28.7) * mm, "end": v(16.5, 27.91) * mm});
            skLineSegment(sketch, "E361", {"start": v(16.5, 27.91) * mm, "end": v(15.53, 27.09) * mm});
            skLineSegment(sketch, "E362", {"start": v(15.53, 27.09) * mm, "end": v(14.66, 26.21) * mm});
            skLineSegment(sketch, "E363", {"start": v(14.66, 26.21) * mm, "end": v(13.83, 26.56) * mm});
            skLineSegment(sketch, "E364", {"start": v(13.83, 26.56) * mm, "end": v(13.03, 26.88) * mm});
            skLineSegment(sketch, "E365", {"start": v(13.03, 26.88) * mm, "end": v(13.02, 28.1) * mm});
            skLineSegment(sketch, "E366", {"start": v(13.02, 28.1) * mm, "end": v(12.91, 29.37) * mm});
            skLineSegment(sketch, "E367", {"start": v(12.91, 29.37) * mm, "end": v(12.71, 30.66) * mm});
            skLineSegment(sketch, "E368", {"start": v(12.71, 30.66) * mm, "end": v(12.43, 31.96) * mm});
            skLineSegment(sketch, "E369", {"start": v(12.43, 31.96) * mm, "end": v(12.06, 33.29) * mm});
            skLineSegment(sketch, "E370", {"start": v(12.06, 33.29) * mm, "end": v(10.89, 33.63) * mm});
            skLineSegment(sketch, "E371", {"start": v(10.89, 33.63) * mm, "end": v(9.87, 32.7) * mm});
            skLineSegment(sketch, "E372", {"start": v(9.87, 32.7) * mm, "end": v(8.93, 31.76) * mm});
            skLineSegment(sketch, "E373", {"start": v(8.93, 31.76) * mm, "end": v(8.07, 30.78) * mm});
            skLineSegment(sketch, "E374", {"start": v(8.07, 30.78) * mm, "end": v(7.3, 29.77) * mm});
            skLineSegment(sketch, "E375", {"start": v(7.3, 29.77) * mm, "end": v(6.64, 28.74) * mm});
            skLineSegment(sketch, "E376", {"start": v(6.64, 28.74) * mm, "end": v(5.75, 28.9) * mm});
            skLineSegment(sketch, "E377", {"start": v(5.75, 28.9) * mm, "end": v(4.9, 29.05) * mm});
            skLineSegment(sketch, "E378", {"start": v(4.9, 29.05) * mm, "end": v(4.64, 30.25) * mm});
            skLineSegment(sketch, "E379", {"start": v(4.64, 30.25) * mm, "end": v(4.27, 31.46) * mm});
            skLineSegment(sketch, "E380", {"start": v(4.27, 31.46) * mm, "end": v(3.8, 32.68) * mm});
            skLineSegment(sketch, "E381", {"start": v(3.8, 32.68) * mm, "end": v(3.26, 33.9) * mm});
            skLineSegment(sketch, "E382", {"start": v(3.26, 33.9) * mm, "end": v(2.62, 35.11) * mm});
            skLineSegment(sketch, "E383", {"start": v(2.62, 35.11) * mm, "end": v(1.4, 35.2) * mm});
            skLineSegment(sketch, "E384", {"start": v(1.4, 35.2) * mm, "end": v(0.6, 34.1) * mm});
            skLineSegment(sketch, "E385", {"start": v(0.6, 34.1) * mm, "end": v(-0.12, 32.97) * mm});
            skLineSegment(sketch, "E386", {"start": v(-0.12, 32.97) * mm, "end": v(-0.76, 31.83) * mm});
            skLineSegment(sketch, "E387", {"start": v(-0.76, 31.83) * mm, "end": v(-1.3, 30.69) * mm});
            skLineSegment(sketch, "E388", {"start": v(-1.3, 30.69) * mm, "end": v(-1.74, 29.54) * mm});
            skLineSegment(sketch, "E389", {"start": v(-1.74, 29.54) * mm, "end": v(-2.64, 29.52) * mm});
            skLineSegment(sketch, "E390", {"start": v(-2.64, 29.52) * mm, "end": v(-3.5, 29.48) * mm});
            skLineSegment(sketch, "E391", {"start": v(-3.5, 29.48) * mm, "end": v(-4, 30.6) * mm});
            skLineSegment(sketch, "E392", {"start": v(-4, 30.6) * mm, "end": v(-4.62, 31.71) * mm});
            skLineSegment(sketch, "E393", {"start": v(-4.62, 31.71) * mm, "end": v(-5.33, 32.8) * mm});
            skLineSegment(sketch, "E394", {"start": v(-5.33, 32.8) * mm, "end": v(-6.12, 33.88) * mm});
            skLineSegment(sketch, "E395", {"start": v(-6.12, 33.88) * mm, "end": v(-7, 34.94) * mm});
            skLineSegment(sketch, "E396", {"start": v(-7, 34.94) * mm, "end": v(-8.2, 34.77) * mm});
            skLineSegment(sketch, "E397", {"start": v(-8.2, 34.77) * mm, "end": v(-8.76, 33.52) * mm});
            skLineSegment(sketch, "E398", {"start": v(-8.76, 33.52) * mm, "end": v(-9.23, 32.27) * mm});
            skLineSegment(sketch, "E399", {"start": v(-9.23, 32.27) * mm, "end": v(-9.61, 31.03) * mm});
            skLineSegment(sketch, "E400", {"start": v(-9.61, 31.03) * mm, "end": v(-9.9, 29.8) * mm});
            skLineSegment(sketch, "E401", {"start": v(-9.9, 29.8) * mm, "end": v(-10.1, 28.58) * mm});
            skLineSegment(sketch, "E402", {"start": v(-10.1, 28.58) * mm, "end": v(-10.98, 28.37) * mm});
            skLineSegment(sketch, "E403", {"start": v(-10.98, 28.37) * mm, "end": v(-11.8, 28.16) * mm});
            skLineSegment(sketch, "E404", {"start": v(-11.8, 28.16) * mm, "end": v(-12.54, 29.15) * mm});
            skLineSegment(sketch, "E405", {"start": v(-12.54, 29.15) * mm, "end": v(-13.37, 30.1) * mm});
            skLineSegment(sketch, "E406", {"start": v(-13.37, 30.1) * mm, "end": v(-14.28, 31.03) * mm});
            skLineSegment(sketch, "E407", {"start": v(-14.28, 31.03) * mm, "end": v(-15.28, 31.92) * mm});
            skLineSegment(sketch, "E408", {"start": v(-15.28, 31.92) * mm, "end": v(-16.36, 32.77) * mm});
            skLineSegment(sketch, "E409", {"start": v(-16.36, 32.77) * mm, "end": v(-17.5, 32.36) * mm});
            skLineSegment(sketch, "E410", {"start": v(-17.5, 32.36) * mm, "end": v(-17.79, 31.02) * mm});
            skLineSegment(sketch, "E411", {"start": v(-17.79, 31.02) * mm, "end": v(-18, 29.7) * mm});
            skLineSegment(sketch, "E412", {"start": v(-18, 29.7) * mm, "end": v(-18.1, 28.4) * mm});
            skLineSegment(sketch, "E413", {"start": v(-18.1, 28.4) * mm, "end": v(-18.14, 27.13) * mm});
            skLineSegment(sketch, "E414", {"start": v(-18.14, 27.13) * mm, "end": v(-18.07, 25.9) * mm});
            skLineSegment(sketch, "E415", {"start": v(-18.07, 25.9) * mm, "end": v(-18.89, 25.52) * mm});
            skLineSegment(sketch, "E416", {"start": v(-18.89, 25.52) * mm, "end": v(-19.66, 25.13) * mm});
            skLineSegment(sketch, "E417", {"start": v(-19.66, 25.13) * mm, "end": v(-20.58, 25.95) * mm});
            skLineSegment(sketch, "E418", {"start": v(-20.58, 25.95) * mm, "end": v(-21.59, 26.72) * mm});
            skLineSegment(sketch, "E419", {"start": v(-21.59, 26.72) * mm, "end": v(-22.68, 27.43) * mm});
            skLineSegment(sketch, "E420", {"start": v(-22.68, 27.43) * mm, "end": v(-23.84, 28.1) * mm});
            skLineSegment(sketch, "E421", {"start": v(-23.84, 28.1) * mm, "end": v(-25.07, 28.7) * mm});
            skLineSegment(sketch, "E422", {"start": v(-25.07, 28.7) * mm, "end": v(-26.1, 28.06) * mm});
            skLineSegment(sketch, "E423", {"start": v(-26.1, 28.06) * mm, "end": v(-26.1, 26.69) * mm});
            skLineSegment(sketch, "E424", {"start": v(-26.1, 26.69) * mm, "end": v(-26.03, 25.35) * mm});
            skLineSegment(sketch, "E425", {"start": v(-26.03, 25.35) * mm, "end": v(-25.87, 24.06) * mm});
            skLineSegment(sketch, "E426", {"start": v(-25.87, 24.06) * mm, "end": v(-25.64, 22.81) * mm});
            skLineSegment(sketch, "E427", {"start": v(-25.64, 22.81) * mm, "end": v(-25.32, 21.62) * mm});
            skLineSegment(sketch, "E428", {"start": v(-25.32, 21.62) * mm, "end": v(-26.04, 21.08) * mm});
            skLineSegment(sketch, "E429", {"start": v(-26.04, 21.08) * mm, "end": v(-26.7, 20.55) * mm});
            skLineSegment(sketch, "E430", {"start": v(-26.7, 20.55) * mm, "end": v(-27.78, 21.15) * mm});
            skLineSegment(sketch, "E431", {"start": v(-27.78, 21.15) * mm, "end": v(-28.93, 21.7) * mm});
            skLineSegment(sketch, "E432", {"start": v(-28.93, 21.7) * mm, "end": v(-30.14, 22.16) * mm});
            skLineSegment(sketch, "E433", {"start": v(-30.14, 22.16) * mm, "end": v(-31.41, 22.57) * mm});
            skLineSegment(sketch, "E434", {"start": v(-31.41, 22.57) * mm, "end": v(-32.74, 22.9) * mm});
            skLineSegment(sketch, "E435", {"start": v(-32.74, 22.9) * mm, "end": v(-33.62, 22.07) * mm});
            skLineSegment(sketch, "E436", {"start": v(-33.62, 22.07) * mm, "end": v(-33.34, 20.72) * mm});
            skLineSegment(sketch, "E437", {"start": v(-33.34, 20.72) * mm, "end": v(-32.98, 19.43) * mm});
            skLineSegment(sketch, "E438", {"start": v(-32.98, 19.43) * mm, "end": v(-32.56, 18.2) * mm});
            skLineSegment(sketch, "E439", {"start": v(-32.56, 18.2) * mm, "end": v(-32.08, 17.03) * mm});
            skLineSegment(sketch, "E440", {"start": v(-32.08, 17.03) * mm, "end": v(-31.51, 15.94) * mm});
            skLineSegment(sketch, "E441", {"start": v(-31.51, 15.94) * mm, "end": v(-32.1, 15.25) * mm});
            skLineSegment(sketch, "E442", {"start": v(-32.1, 15.25) * mm, "end": v(-32.65, 14.6) * mm});
            skLineSegment(sketch, "E443", {"start": v(-32.65, 14.6) * mm, "end": v(-33.83, 14.96) * mm});
            skLineSegment(sketch, "E444", {"start": v(-33.83, 14.96) * mm, "end": v(-35.06, 15.25) * mm});
            skLineSegment(sketch, "E445", {"start": v(-35.06, 15.25) * mm, "end": v(-36.34, 15.46) * mm});
            skLineSegment(sketch, "E446", {"start": v(-36.34, 15.46) * mm, "end": v(-37.67, 15.6) * mm});
            skLineSegment(sketch, "E447", {"start": v(-37.67, 15.6) * mm, "end": v(-39.04, 15.65) * mm});
            skLineSegment(sketch, "E448", {"start": v(-39.04, 15.65) * mm, "end": v(-39.73, 14.64) * mm});
            skLineSegment(sketch, "E449", {"start": v(-39.73, 14.64) * mm, "end": v(-39.17, 13.39) * mm});
            skLineSegment(sketch, "E450", {"start": v(-39.17, 13.39) * mm, "end": v(-38.56, 12.2) * mm});
            skLineSegment(sketch, "E451", {"start": v(-38.56, 12.2) * mm, "end": v(-37.9, 11.08) * mm});
            skLineSegment(sketch, "E452", {"start": v(-37.9, 11.08) * mm, "end": v(-37.17, 10.04) * mm});
            skLineSegment(sketch, "E453", {"start": v(-37.17, 10.04) * mm, "end": v(-36.4, 9.08) * mm});
            skLineSegment(sketch, "E454", {"start": v(-36.4, 9.08) * mm, "end": v(-36.83, 8.3) * mm});
            skLineSegment(sketch, "E455", {"start": v(-36.83, 8.3) * mm, "end": v(-37.23, 7.53) * mm});
            skLineSegment(sketch, "E456", {"start": v(-37.23, 7.53) * mm, "end": v(-38.45, 7.65) * mm});
            skLineSegment(sketch, "E457", {"start": v(-38.45, 7.65) * mm, "end": v(-39.72, 7.68) * mm});
            skLineSegment(sketch, "E458", {"start": v(-39.72, 7.68) * mm, "end": v(-41.02, 7.61) * mm});
            skLineSegment(sketch, "E459", {"start": v(-41.02, 7.61) * mm, "end": v(-42.35, 7.46) * mm});
            skLineSegment(sketch, "E460", {"start": v(-42.35, 7.46) * mm, "end": v(-43.7, 7.24) * mm});
            skLineSegment(sketch, "E461", {"start": v(-43.7, 7.24) * mm, "end": v(-44.16, 6.1) * mm});
            skLineSegment(sketch, "E462", {"start": v(-44.16, 6.1) * mm, "end": v(-43.35, 5) * mm});
            skLineSegment(sketch, "E463", {"start": v(-43.35, 5) * mm, "end": v(-42.5, 3.96) * mm});
            skLineSegment(sketch, "E464", {"start": v(-42.5, 3.96) * mm, "end": v(-41.62, 3) * mm});
            skLineSegment(sketch, "E465", {"start": v(-41.62, 3) * mm, "end": v(-40.7, 2.14) * mm});
            skLineSegment(sketch, "E466", {"start": v(-40.7, 2.14) * mm, "end": v(-39.74, 1.37) * mm});
            skLineSegment(sketch, "E467", {"start": v(-39.74, 1.37) * mm, "end": v(-40, 0.5) * mm});
            skLineSegment(sketch, "E468", {"start": v(-40, 0.5) * mm, "end": v(-40.23, -0.32) * mm});
            skLineSegment(sketch, "E469", {"start": v(-40.23, -0.32) * mm, "end": v(-41.46, -0.46) * mm});
            skLineSegment(sketch, "E470", {"start": v(-41.46, -0.46) * mm, "end": v(-42.7, -0.7) * mm});
            skLineSegment(sketch, "E471", {"start": v(-42.7, -0.7) * mm, "end": v(-43.96, -1.03) * mm});
            skLineSegment(sketch, "E472", {"start": v(-43.96, -1.03) * mm, "end": v(-45.23, -1.46) * mm});
            skLineSegment(sketch, "E473", {"start": v(-45.23, -1.46) * mm, "end": v(-46.5, -1.96) * mm});
            skLineSegment(sketch, "E474", {"start": v(-46.5, -1.96) * mm, "end": v(-46.72, -3.16) * mm});
            skLineSegment(sketch, "E475", {"start": v(-46.72, -3.16) * mm, "end": v(-45.7, -4.08) * mm});
            skLineSegment(sketch, "E476", {"start": v(-45.7, -4.08) * mm, "end": v(-44.66, -4.91) * mm});
            skLineSegment(sketch, "E477", {"start": v(-44.66, -4.91) * mm, "end": v(-43.6, -5.66) * mm});
            skLineSegment(sketch, "E478", {"start": v(-43.6, -5.66) * mm, "end": v(-42.51, -6.32) * mm});
            skLineSegment(sketch, "E479", {"start": v(-42.51, -6.32) * mm, "end": v(-41.41, -6.88) * mm});
            skLineSegment(sketch, "E480", {"start": v(-41.41, -6.88) * mm, "end": v(-41.49, -7.78) * mm});
            skLineSegment(sketch, "E481", {"start": v(-41.49, -7.78) * mm, "end": v(-41.54, -8.63) * mm});
            skLineSegment(sketch, "E482", {"start": v(-41.54, -8.63) * mm, "end": v(-42.7, -9.02) * mm});
            skLineSegment(sketch, "E483", {"start": v(-42.7, -9.02) * mm, "end": v(-43.88, -9.52) * mm});
            skLineSegment(sketch, "E484", {"start": v(-43.88, -9.52) * mm, "end": v(-45.04, -10.1) * mm});
            skLineSegment(sketch, "E485", {"start": v(-45.04, -10.1) * mm, "end": v(-46.2, -10.78) * mm});
            skLineSegment(sketch, "E486", {"start": v(-46.2, -10.78) * mm, "end": v(-47.33, -11.54) * mm});
            skLineSegment(sketch, "E487", {"start": v(-47.33, -11.54) * mm, "end": v(-47.3, -12.76) * mm});
            skLineSegment(sketch, "E488", {"start": v(-47.3, -12.76) * mm, "end": v(-46.1, -13.44) * mm});
            skLineSegment(sketch, "E489", {"start": v(-46.1, -13.44) * mm, "end": v(-44.92, -14.04) * mm});
            skLineSegment(sketch, "E490", {"start": v(-44.92, -14.04) * mm, "end": v(-43.72, -14.56) * mm});
            skLineSegment(sketch, "E491", {"start": v(-43.72, -14.56) * mm, "end": v(-42.52, -14.97) * mm});
            skLineSegment(sketch, "E492", {"start": v(-42.52, -14.97) * mm, "end": v(-41.33, -15.3) * mm});
            skLineSegment(sketch, "E493", {"start": v(-41.33, -15.3) * mm, "end": v(-41.22, -16.19) * mm});
            skLineSegment(sketch, "E494", {"start": v(-41.22, -16.19) * mm, "end": v(-41.1, -17.03) * mm});
            skLineSegment(sketch, "E495", {"start": v(-41.1, -17.03) * mm, "end": v(-42.15, -17.66) * mm});
            skLineSegment(sketch, "E496", {"start": v(-42.15, -17.66) * mm, "end": v(-43.2, -18.38) * mm});
            skLineSegment(sketch, "E497", {"start": v(-43.2, -18.38) * mm, "end": v(-44.2, -19.2) * mm});
            skLineSegment(sketch, "E498", {"start": v(-44.2, -19.2) * mm, "end": v(-45.2, -20.1) * mm});
            skLineSegment(sketch, "E499", {"start": v(-45.2, -20.1) * mm, "end": v(-46.16, -21.08) * mm});
            skLineSegment(sketch, "E500", {"start": v(-46.16, -21.08) * mm, "end": v(-45.87, -22.26) * mm});
            skLineSegment(sketch, "E501", {"start": v(-45.87, -22.26) * mm, "end": v(-44.56, -22.69) * mm});
            skLineSegment(sketch, "E502", {"start": v(-44.56, -22.69) * mm, "end": v(-43.27, -23.03) * mm});
            skLineSegment(sketch, "E503", {"start": v(-43.27, -23.03) * mm, "end": v(-42, -23.28) * mm});
            skLineSegment(sketch, "E504", {"start": v(-42, -23.28) * mm, "end": v(-40.73, -23.44) * mm});
            skLineSegment(sketch, "E505", {"start": v(-40.73, -23.44) * mm, "end": v(-39.5, -23.5) * mm});
            skLineSegment(sketch, "E506", {"start": v(-39.5, -23.5) * mm, "end": v(-39.2, -24.36) * mm});
            skLineSegment(sketch, "E507", {"start": v(-39.2, -24.36) * mm, "end": v(-38.9, -25.16) * mm});
            skLineSegment(sketch, "E508", {"start": v(-38.9, -25.16) * mm, "end": v(-39.82, -26) * mm});
            skLineSegment(sketch, "E509", {"start": v(-39.82, -26) * mm, "end": v(-40.68, -26.92) * mm});
            skLineSegment(sketch, "E510", {"start": v(-40.68, -26.92) * mm, "end": v(-41.5, -27.92) * mm});
            skLineSegment(sketch, "E511", {"start": v(-41.5, -27.92) * mm, "end": v(-42.29, -29.01) * mm});
            skLineSegment(sketch, "E512", {"start": v(-42.29, -29.01) * mm, "end": v(-43.02, -30.17) * mm});
            skLineSegment(sketch, "E513", {"start": v(-43.02, -30.17) * mm, "end": v(-42.49, -31.26) * mm});
            skLineSegment(sketch, "E514", {"start": v(-42.49, -31.26) * mm, "end": v(-41.13, -31.4) * mm});
            skLineSegment(sketch, "E515", {"start": v(-41.13, -31.4) * mm, "end": v(-39.8, -31.47) * mm});
            skLineSegment(sketch, "E516", {"start": v(-39.8, -31.47) * mm, "end": v(-38.49, -31.45) * mm});
            skLineSegment(sketch, "E517", {"start": v(-38.49, -31.45) * mm, "end": v(-37.23, -31.35) * mm});
            skLineSegment(sketch, "E518", {"start": v(-37.23, -31.35) * mm, "end": v(-36, -31.15) * mm});
            skLineSegment(sketch, "E519", {"start": v(-36, -31.15) * mm, "end": v(-35.54, -31.93) * mm});
            skLineSegment(sketch, "E520", {"start": v(-35.54, -31.93) * mm, "end": v(-35.08, -32.65) * mm});
            skLineSegment(sketch, "E521", {"start": v(-35.08, -32.65) * mm, "end": v(-35.8, -33.65) * mm});
            skLineSegment(sketch, "E522", {"start": v(-35.8, -33.65) * mm, "end": v(-36.45, -34.74) * mm});
            skLineSegment(sketch, "E523", {"start": v(-36.45, -34.74) * mm, "end": v(-37.05, -35.9) * mm});
            skLineSegment(sketch, "E524", {"start": v(-37.05, -35.9) * mm, "end": v(-37.58, -37.12) * mm});
            skLineSegment(sketch, "E525", {"start": v(-37.58, -37.12) * mm, "end": v(-38.06, -38.4) * mm});
            skLineSegment(sketch, "E526", {"start": v(-38.06, -38.4) * mm, "end": v(-37.32, -39.37) * mm});
            skLineSegment(sketch, "E527", {"start": v(-37.32, -39.37) * mm, "end": v(-35.95, -39.22) * mm});
            skLineSegment(sketch, "E528", {"start": v(-35.95, -39.22) * mm, "end": v(-34.63, -39) * mm});
            skLineSegment(sketch, "E529", {"start": v(-34.63, -39) * mm, "end": v(-33.36, -38.72) * mm});
            skLineSegment(sketch, "E530", {"start": v(-33.36, -38.72) * mm, "end": v(-32.15, -38.36) * mm});
            skLineSegment(sketch, "E531", {"start": v(-32.15, -38.36) * mm, "end": v(-31, -37.91) * mm});
            skLineSegment(sketch, "E532", {"start": v(-31, -37.91) * mm, "end": v(-30.38, -38.57) * mm});
            skLineSegment(sketch, "E533", {"start": v(-30.38, -38.57) * mm, "end": v(-29.78, -39.18) * mm});
            skLineSegment(sketch, "E534", {"start": v(-29.78, -39.18) * mm, "end": v(-30.27, -40.31) * mm});
            skLineSegment(sketch, "E535", {"start": v(-30.27, -40.31) * mm, "end": v(-30.69, -41.5) * mm});
            skLineSegment(sketch, "E536", {"start": v(-30.69, -41.5) * mm, "end": v(-31.03, -42.77) * mm});
            skLineSegment(sketch, "E537", {"start": v(-31.03, -42.77) * mm, "end": v(-31.3, -44.08) * mm});
            skLineSegment(sketch, "E538", {"start": v(-31.3, -44.08) * mm, "end": v(-31.5, -45.43) * mm});
            skLineSegment(sketch, "E539", {"start": v(-31.5, -45.43) * mm, "end": v(-30.57, -46.22) * mm});
            skLineSegment(sketch, "E540", {"start": v(-30.57, -46.22) * mm, "end": v(-29.27, -45.8) * mm});
            skLineSegment(sketch, "E541", {"start": v(-29.27, -45.8) * mm, "end": v(-28.02, -45.3) * mm});
            skLineSegment(sketch, "E542", {"start": v(-28.02, -45.3) * mm, "end": v(-26.84, -44.76) * mm});
            skLineSegment(sketch, "E543", {"start": v(-26.84, -44.76) * mm, "end": v(-25.73, -44.15) * mm});
            skLineSegment(sketch, "E544", {"start": v(-25.73, -44.15) * mm, "end": v(-24.7, -43.48) * mm});
            skLineSegment(sketch, "E545", {"start": v(-24.7, -43.48) * mm, "end": v(-23.95, -44) * mm});
            skLineSegment(sketch, "E546", {"start": v(-23.95, -44) * mm, "end": v(-23.24, -44.47) * mm});
            skLineSegment(sketch, "E547", {"start": v(-23.24, -44.47) * mm, "end": v(-23.49, -45.68) * mm});
            skLineSegment(sketch, "E548", {"start": v(-23.49, -45.68) * mm, "end": v(-23.64, -46.94) * mm});
            skLineSegment(sketch, "E549", {"start": v(-23.64, -46.94) * mm, "end": v(-23.71, -48.24) * mm});
            skLineSegment(sketch, "E550", {"start": v(-23.71, -48.24) * mm, "end": v(-23.7, -49.57) * mm});
            skLineSegment(sketch, "E551", {"start": v(-23.7, -49.57) * mm, "end": v(-23.62, -50.94) * mm});
            skLineSegment(sketch, "E552", {"start": v(-23.62, -50.94) * mm, "end": v(-22.55, -51.52) * mm});
            skLineSegment(sketch, "E553", {"start": v(-22.55, -51.52) * mm, "end": v(-21.36, -50.83) * mm});
            skLineSegment(sketch, "E554", {"start": v(-21.36, -50.83) * mm, "end": v(-20.24, -50.1) * mm});
            skLineSegment(sketch, "E555", {"start": v(-20.24, -50.1) * mm, "end": v(-19.2, -49.32) * mm});
            skLineSegment(sketch, "E556", {"start": v(-19.2, -49.32) * mm, "end": v(-18.24, -48.5) * mm});
            skLineSegment(sketch, "E557", {"start": v(-18.24, -48.5) * mm, "end": v(-17.37, -47.62) * mm});
            skLineSegment(sketch, "E558", {"start": v(-17.37, -47.62) * mm, "end": v(-16.54, -47.97) * mm});
            skLineSegment(sketch, "E559", {"start": v(-16.54, -47.97) * mm, "end": v(-15.74, -48.28) * mm});
            skLineSegment(sketch, "E560", {"start": v(-15.74, -48.28) * mm, "end": v(-15.73, -49.52) * mm});
            skLineSegment(sketch, "E561", {"start": v(-15.73, -49.52) * mm, "end": v(-15.62, -50.78) * mm});
            skLineSegment(sketch, "E562", {"start": v(-15.62, -50.78) * mm, "end": v(-15.42, -52.06) * mm});
            skLineSegment(sketch, "E563", {"start": v(-15.42, -52.06) * mm, "end": v(-15.14, -53.37) * mm});
            skLineSegment(sketch, "E564", {"start": v(-15.14, -53.37) * mm, "end": v(-14.77, -54.7) * mm});
            skLineSegment(sketch, "E565", {"start": v(-14.77, -54.7) * mm, "end": v(-13.6, -55.03) * mm});
            skLineSegment(sketch, "E566", {"start": v(-13.6, -55.03) * mm, "end": v(-12.58, -54.11) * mm});
            skLineSegment(sketch, "E567", {"start": v(-12.58, -54.11) * mm, "end": v(-11.64, -53.16) * mm});
            skLineSegment(sketch, "E568", {"start": v(-11.64, -53.16) * mm, "end": v(-10.78, -52.18) * mm});
            skLineSegment(sketch, "E569", {"start": v(-10.78, -52.18) * mm, "end": v(-10.01, -51.18) * mm});
            skLineSegment(sketch, "E570", {"start": v(-10.01, -51.18) * mm, "end": v(-9.34, -50.14) * mm});
            skLineSegment(sketch, "E571", {"start": v(-9.34, -50.14) * mm, "end": v(-8.46, -50.3) * mm});
            skLineSegment(sketch, "E572", {"start": v(-8.46, -50.3) * mm, "end": v(-7.61, -50.45) * mm});
            skLineSegment(sketch, "E573", {"start": v(-7.61, -50.45) * mm, "end": v(-7.35, -51.66) * mm});
            skLineSegment(sketch, "E574", {"start": v(-7.35, -51.66) * mm, "end": v(-6.98, -52.87) * mm});
            skLineSegment(sketch, "E575", {"start": v(-6.98, -52.87) * mm, "end": v(-6.52, -54.09) * mm});
            skLineSegment(sketch, "E576", {"start": v(-6.52, -54.09) * mm, "end": v(-5.96, -55.3) * mm});
            skLineSegment(sketch, "E577", {"start": v(-5.96, -55.3) * mm, "end": v(-5.33, -56.52) * mm});
            skLineSegment(sketch, "E578", {"start": v(-5.33, -56.52) * mm, "end": v(-4.11, -56.6) * mm});
            skLineSegment(sketch, "E579", {"start": v(-4.11, -56.6) * mm, "end": v(-3.3, -55.5) * mm});
            skLineSegment(sketch, "E580", {"start": v(69.98, -57.7) * mm, "end": v(67, -57.7) * mm});
            skLineSegment(sketch, "E581", {"start": v(67, -57.7) * mm, "end": v(63.93, -51.95) * mm});
            skLineSegment(sketch, "E582", {"start": v(63.93, -51.95) * mm, "end": v(62.49, -51.95) * mm});
            skLineSegment(sketch, "E583", {"start": v(62.49, -51.95) * mm, "end": v(59.42, -57.7) * mm});
            skLineSegment(sketch, "E584", {"start": v(59.42, -57.7) * mm, "end": v(57.97, -57.7) * mm});
            skLineSegment(sketch, "E585", {"start": v(57.97, -57.7) * mm, "end": v(54.9, -51.95) * mm});
            skLineSegment(sketch, "E586", {"start": v(54.9, -51.95) * mm, "end": v(53.46, -51.95) * mm});
            skLineSegment(sketch, "E587", {"start": v(53.46, -51.95) * mm, "end": v(50.39, -57.7) * mm});
            skLineSegment(sketch, "E588", {"start": v(50.39, -57.7) * mm, "end": v(48.94, -57.7) * mm});
            skLineSegment(sketch, "E589", {"start": v(48.94, -57.7) * mm, "end": v(45.87, -51.95) * mm});
            skLineSegment(sketch, "E590", {"start": v(45.87, -51.95) * mm, "end": v(44.43, -51.95) * mm});
            skLineSegment(sketch, "E591", {"start": v(44.43, -51.95) * mm, "end": v(41.36, -57.7) * mm});
            skLineSegment(sketch, "E592", {"start": v(41.36, -57.7) * mm, "end": v(39.91, -57.7) * mm});
            skLineSegment(sketch, "E593", {"start": v(39.91, -57.7) * mm, "end": v(36.84, -51.95) * mm});
            skLineSegment(sketch, "E594", {"start": v(36.84, -51.95) * mm, "end": v(35.4, -51.95) * mm});
            skLineSegment(sketch, "E595", {"start": v(35.4, -51.95) * mm, "end": v(32.33, -57.7) * mm});
            skLineSegment(sketch, "E596", {"start": v(32.33, -57.7) * mm, "end": v(30.88, -57.7) * mm});
            skLineSegment(sketch, "E597", {"start": v(30.88, -57.7) * mm, "end": v(27.81, -51.95) * mm});
            skLineSegment(sketch, "E598", {"start": v(27.81, -51.95) * mm, "end": v(26.37, -51.95) * mm});
            skLineSegment(sketch, "E599", {"start": v(26.37, -51.95) * mm, "end": v(23.3, -57.7) * mm});
            skLineSegment(sketch, "E600", {"start": v(23.3, -57.7) * mm, "end": v(21.85, -57.7) * mm});
            skLineSegment(sketch, "E601", {"start": v(21.85, -57.7) * mm, "end": v(18.78, -51.95) * mm});
            skLineSegment(sketch, "E602", {"start": v(18.78, -51.95) * mm, "end": v(17.34, -51.95) * mm});
            skLineSegment(sketch, "E603", {"start": v(17.34, -51.95) * mm, "end": v(14.27, -57.7) * mm});
            skLineSegment(sketch, "E604", {"start": v(14.27, -57.7) * mm, "end": v(12.82, -57.7) * mm});
            skLineSegment(sketch, "E605", {"start": v(12.82, -57.7) * mm, "end": v(9.75, -51.95) * mm});
            skLineSegment(sketch, "E606", {"start": v(9.75, -51.95) * mm, "end": v(8.3, -51.95) * mm});
            skLineSegment(sketch, "E607", {"start": v(8.3, -51.95) * mm, "end": v(5.24, -57.7) * mm});
            skLineSegment(sketch, "E608", {"start": v(5.24, -57.7) * mm, "end": v(3.8, -57.7) * mm});
            skLineSegment(sketch, "E609", {"start": v(3.8, -57.7) * mm, "end": v(0.72, -51.95) * mm});
            skLineSegment(sketch, "E610", {"start": v(0.72, -51.95) * mm, "end": v(-0.72, -51.95) * mm});
            skLineSegment(sketch, "E611", {"start": v(-0.72, -51.95) * mm, "end": v(-3.8, -57.7) * mm});
            skLineSegment(sketch, "E612", {"start": v(-3.8, -57.7) * mm, "end": v(-5.24, -57.7) * mm});
            skLineSegment(sketch, "E613", {"start": v(-5.24, -57.7) * mm, "end": v(-8.3, -51.95) * mm});
            skLineSegment(sketch, "E614", {"start": v(-8.3, -51.95) * mm, "end": v(-9.75, -51.95) * mm});
            skLineSegment(sketch, "E615", {"start": v(-9.75, -51.95) * mm, "end": v(-12.82, -57.7) * mm});
            skLineSegment(sketch, "E616", {"start": v(-12.82, -57.7) * mm, "end": v(-14.27, -57.7) * mm});
            skLineSegment(sketch, "E617", {"start": v(-14.27, -57.7) * mm, "end": v(-17.34, -51.95) * mm});
            skLineSegment(sketch, "E618", {"start": v(-17.34, -51.95) * mm, "end": v(-18.78, -51.95) * mm});
            skLineSegment(sketch, "E619", {"start": v(-18.78, -51.95) * mm, "end": v(-21.85, -57.7) * mm});
            skLineSegment(sketch, "E620", {"start": v(-21.85, -57.7) * mm, "end": v(-23.3, -57.7) * mm});
            skLineSegment(sketch, "E621", {"start": v(-23.3, -57.7) * mm, "end": v(-26.37, -51.95) * mm});
            skLineSegment(sketch, "E622", {"start": v(-26.37, -51.95) * mm, "end": v(-27.81, -51.95) * mm});
            skLineSegment(sketch, "E623", {"start": v(-27.81, -51.95) * mm, "end": v(-30.88, -57.7) * mm});
            skLineSegment(sketch, "E624", {"start": v(-30.88, -57.7) * mm, "end": v(-32.33, -57.7) * mm});
            skLineSegment(sketch, "E625", {"start": v(-32.33, -57.7) * mm, "end": v(-35.4, -51.95) * mm});
            skLineSegment(sketch, "E626", {"start": v(-35.4, -51.95) * mm, "end": v(-36.84, -51.95) * mm});
            skLineSegment(sketch, "E627", {"start": v(-36.84, -51.95) * mm, "end": v(-39.91, -57.7) * mm});
            skLineSegment(sketch, "E628", {"start": v(-39.91, -57.7) * mm, "end": v(-41.36, -57.7) * mm});
            skLineSegment(sketch, "E629", {"start": v(-41.36, -57.7) * mm, "end": v(-44.43, -51.95) * mm});
            skLineSegment(sketch, "E630", {"start": v(-44.43, -51.95) * mm, "end": v(-45.87, -51.95) * mm});
            skLineSegment(sketch, "E631", {"start": v(-45.87, -51.95) * mm, "end": v(-48.94, -57.7) * mm});
            skLineSegment(sketch, "E632", {"start": v(-48.94, -57.7) * mm, "end": v(-50.39, -57.7) * mm});
            skLineSegment(sketch, "E633", {"start": v(-50.39, -57.7) * mm, "end": v(-53.46, -51.95) * mm});
            skLineSegment(sketch, "E634", {"start": v(-53.46, -51.95) * mm, "end": v(-54.9, -51.95) * mm});
            skLineSegment(sketch, "E635", {"start": v(-54.9, -51.95) * mm, "end": v(-57.97, -57.7) * mm});
            skLineSegment(sketch, "E636", {"start": v(-57.97, -57.7) * mm, "end": v(-59.42, -57.7) * mm});
            skLineSegment(sketch, "E637", {"start": v(-59.42, -57.7) * mm, "end": v(-62.49, -51.95) * mm});
            skLineSegment(sketch, "E638", {"start": v(-62.49, -51.95) * mm, "end": v(-63.93, -51.95) * mm});
            skLineSegment(sketch, "E639", {"start": v(-63.93, -51.95) * mm, "end": v(-67, -57.7) * mm});
            skLineSegment(sketch, "E640", {"start": v(-67, -57.7) * mm, "end": v(-69.98, -57.7) * mm});
            skLineSegment(sketch, "E641", {"start": v(-69.98, -57.7) * mm, "end": v(-69.98, -63.99) * mm});
            skLineSegment(sketch, "E642", {"start": v(-69.98, -63.99) * mm, "end": v(69.98, -63.99) * mm});
            skLineSegment(sketch, "E643", {"start": v(69.98, -63.99) * mm, "end": v(69.98, -57.7) * mm});
            skLineSegment(sketch, "E644", {"start": v(-3.66, 47.78) * mm, "end": v(0.95, 45.79) * mm, "construction": true});
            skLineSegment(sketch, "E645", {"start": v(-0.36, 49.08) * mm, "end": v(-2.35, 44.48) * mm, "construction": true});
            skPoint(sketch, "E646", {"position": v(-1.35, 46.78) * mm});
            skCircle(sketch, "E647", {"center": v(-1.35, 46.78) * mm, "radius": 2.5 * mm});
            skLineSegment(sketch, "E648", {"start": v(-1.7, -8.22) * mm, "end": v(-1.01, -13.19) * mm, "construction": true});
            skLineSegment(sketch, "E649", {"start": v(1.13, -10.36) * mm, "end": v(-3.84, -11.04) * mm, "construction": true});
            skPoint(sketch, "E650", {"position": v(-1.35, -10.7) * mm});
            skCircle(sketch, "E651", {"center": v(-1.35, -10.7) * mm, "radius": 3.18 * mm});
            skSolve(sketch);
        }
        {
            var Q0;
            Q0 = qSketchRegion(id + "F0", true);
            extrude(context, id + "F1", {"entities" : qUnion([Q0]), "depth" : 12.7 * mm, "offsetDistance" : 25.4 * mm});
        }
        {
            var Q0;
            Q0=makeQuery(id+"F0.imprint","IMPRINT",FACE,{"disambiguationData":[TD([[makeQuery(id+"F0.imprint","IMPRINT",EDGE,{"derivedFrom":sQuery(id+"F0.wireOp",EDGE,"E651")}),1.0]])]});
            var Q1;
            Q1=sQuery(id+"F0.wireOp",EDGE,"E651");
            extrude(context, id + "F2", {"entities" : qUnion([Q0]), "surfaceEntities" : qUnion([Q1]), "depth" : 50.8 * mm, "offsetDistance" : 25.4 * mm});
        }
        {
            var Q0;
            Q0=makeQuery(id+"F1.opExtrude","SWEPT_FACE",FACE,{"disambiguationData":[OSD([sQuery(id+"F0.wireOp",EDGE,"E642")])]});
            var sketch = newSketch(context, id + "F3", { "sketchPlane" : qUnion([Q0])});
            skLineSegment(sketch, "E652.bottom", {"start": v(-69.98, -44.45) * mm, "end": v(69.98, -44.45) * mm});
            skLineSegment(sketch, "E652.top", {"start": v(-69.98, 57.15) * mm, "end": v(69.98, 57.15) * mm});
            skLineSegment(sketch, "E652.left", {"start": v(-69.98, -44.45) * mm, "end": v(-69.98, 57.15) * mm});
            skLineSegment(sketch, "E652.right", {"start": v(69.98, -44.45) * mm, "end": v(69.98, 57.15) * mm});
            skPoint(sketch, "E652.middle", {"position": v(0, 6.35) * mm});
            skPoint(sketch, "E652.middle.positionSnap0", {"position": v(-69.98, 6.35) * mm});
            skPoint(sketch, "E652.middle.positionSnap1", {"position": v(0, 0) * mm});
            skPoint(sketch, "E652.cornerSnap0", {"position": v(-69.98, 6.35) * mm});
            skPoint(sketch, "E652.centerSnap0", {"position": v(-69.98, 6.35) * mm});
            skPoint(sketch, "E652.centerSnap1", {"position": v(0, 0) * mm});
            skSolve(sketch);
        }
        {
            var Q0;
            Q0 = qSketchRegion(id + "F3", true);
            extrude(context, id + "F4", {"entities" : qUnion([Q0]), "depth" : 1 / 406.4 * mm, "offsetDistance" : 25.4 * mm});
        }
    });
